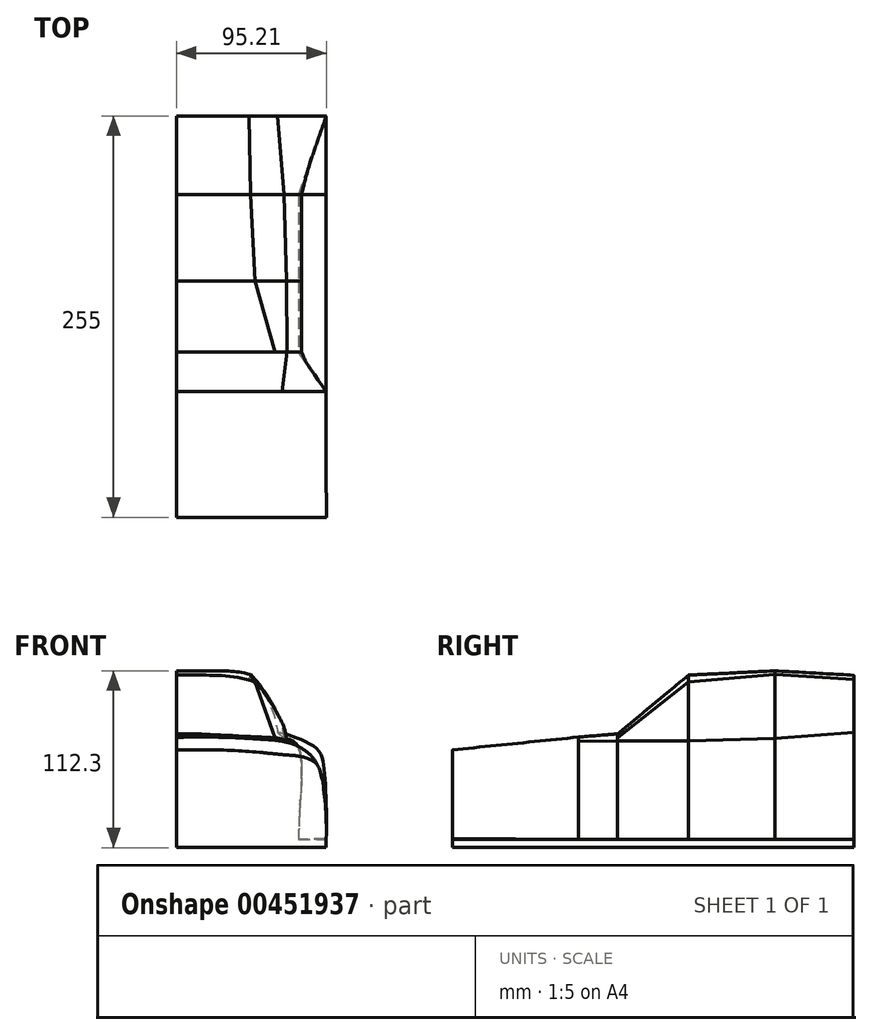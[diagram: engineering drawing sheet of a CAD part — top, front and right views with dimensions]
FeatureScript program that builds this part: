
annotation { "Feature Type Name" : "Feature", "Feature Type Description" : "" }
export const myFeature = defineFeature(function(context is Context, id is Id, definition is map)
    precondition{}
    {
        {
            var Q0;
            Q0=qCreatedBy(makeId("Front.planeOp"),FACE);
            cPlane(context, id + "F0", {"entities" : qUnion([Q0]), "cplaneType" : CPlaneType.OFFSET, "offset" : 25 * mm, "width" : 150 * mm, "height" : 150 * mm});
        }
        {
            var Q0;
            Q0=qCreatedBy(id+"F0.planeOp",FACE);
            cPlane(context, id + "F1", {"entities" : qUnion([Q0]), "cplaneType" : CPlaneType.OFFSET, "offset" : 55 * mm, "width" : 150 * mm, "height" : 150 * mm});
        }
        {
            var Q0;
            Q0=qCreatedBy(id+"F1.planeOp",FACE);
            var sketch = newSketch(context, id + "F2", { "sketchPlane" : qUnion([Q0])});
            skLineSegment(sketch, "E0", {"start": v(-56.2, -43.48) * mm, "end": v(38.8, -43.48) * mm});
            skLineSegment(sketch, "E1", {"start": v(-56.2, -43.48) * mm, "end": v(-56.2, 68.52) * mm});
            skFitSpline(sketch, "E2", {"points": [v(-56.2, 68.52) * mm, v(-28.09, 68.52) * mm, v(-9.15, 66.18) * mm], "startDerivative": vector(14.34, 0) * mm, "endDerivative": vector(49, -12.81) * mm});
            skFitSpline(sketch, "E3", {"points": [v(-9.15, 66.18) * mm, v(3.27, 49.99) * mm, v(10.5, 34.27) * mm, v(12.07, 25.62) * mm], "startDerivative": vector(39.03, -40.53) * mm, "endDerivative": vector(5.17, -25.63) * mm});
            skFitSpline(sketch, "E4", {"points": [v(12.07, 25.62) * mm, v(18.99, 23.1) * mm, v(23.1, 11.29) * mm, v(22.4, -13.75) * mm, v(21.25, -38.41) * mm], "startDerivative": vector(44.42, -4.76) * mm, "endDerivative": vector(-3.51, -107.92) * mm});
            skFitSpline(sketch, "E5", {"points": [v(21.25, -38.41) * mm, v(38.7, -38.41) * mm], "startDerivative": vector(17.45, 0) * mm, "endDerivative": vector(17.45, 0) * mm});
            skFitSpline(sketch, "E6", {"points": [v(38.7, -38.41) * mm, v(38.8, -43.48) * mm], "startDerivative": vector(0.15, -5.07) * mm, "endDerivative": vector(0.15, -5.07) * mm});
            skSolve(sketch);
        }
        {
            var Q0;
            Q0=qCreatedBy(id+"F1.planeOp",FACE);
            cPlane(context, id + "F3", {"entities" : qUnion([Q0]), "cplaneType" : CPlaneType.OFFSET, "offset" : 55 * mm, "width" : 150 * mm, "height" : 150 * mm});
        }
        {
            var Q0;
            Q0=qCreatedBy(id+"F3.planeOp",FACE);
            var sketch = newSketch(context, id + "F4", { "sketchPlane" : qUnion([Q0])});
            skLineSegment(sketch, "E7", {"start": v(-56.24, -43.48) * mm, "end": v(38.76, -43.48) * mm});
            skLineSegment(sketch, "E8", {"start": v(-56.24, -43.48) * mm, "end": v(-56.24, 65.86) * mm});
            skFitSpline(sketch, "E9", {"points": [v(-56.24, 65.86) * mm, v(-42, 65.86) * mm, v(-6.36, 61.62) * mm], "startDerivative": vector(26.6, 0) * mm, "endDerivative": vector(61.7, -20.82) * mm});
            skFitSpline(sketch, "E10", {"points": [v(-6.36, 61.62) * mm, v(2.01, 51.09) * mm, v(12.26, 32.17) * mm, v(13.8, 24.2) * mm], "startDerivative": vector(39.03, -40.53) * mm, "endDerivative": vector(5.17, -25.63) * mm});
            skFitSpline(sketch, "E11", {"points": [v(13.8, 24.2) * mm, v(20.09, 22) * mm, v(23.1, 11.29) * mm, v(22.4, -13.75) * mm, v(21.17, -38.41) * mm], "startDerivative": vector(44.42, -4.76) * mm, "endDerivative": vector(-3.51, -107.92) * mm});
            skFitSpline(sketch, "E12", {"points": [v(21.17, -38.41) * mm, v(38.7, -38.41) * mm], "startDerivative": vector(17.45, 0) * mm, "endDerivative": vector(17.45, 0) * mm});
            skFitSpline(sketch, "E13", {"points": [v(38.7, -38.41) * mm, v(38.76, -43.48) * mm], "startDerivative": vector(0.15, -5.07) * mm, "endDerivative": vector(0.15, -5.07) * mm});
            skSolve(sketch);
        }
        {
            var Q0;
            Q0=makeQuery(id+"F2.imprint","IMPRINT",FACE,{"disambiguationData":[TD([[makeQuery(id+"F2.imprint","IMPRINT",EDGE,{"derivedFrom":sQuery(id+"F2.wireOp",EDGE,"E0")}),1.0]])]});
            var Q1;
            Q1=makeQuery(id+"F4.imprint","IMPRINT",FACE,{"disambiguationData":[TD([[makeQuery(id+"F4.imprint","IMPRINT",EDGE,{"derivedFrom":sQuery(id+"F4.wireOp",EDGE,"E7")}),1.0]])]});
            loft(context, id + "F5", {"sheetProfilesArray" : [{ "sheetProfileEntities" : qUnion([Q0]) }, { "sheetProfileEntities" : qUnion([Q1]) }]});
        }
        {
            var Q0;
            Q0=qCreatedBy(id+"F3.planeOp",FACE);
            cPlane(context, id + "F6", {"entities" : qUnion([Q0]), "cplaneType" : CPlaneType.OFFSET, "offset" : 45 * mm, "width" : 150 * mm, "height" : 150 * mm});
        }
        {
            var Q0;
            Q0=qCreatedBy(id+"F6.planeOp",FACE);
            var sketch = newSketch(context, id + "F7", { "sketchPlane" : qUnion([Q0])});
            skLineSegment(sketch, "E14", {"start": v(-56.16, -43.48) * mm, "end": v(38.84, -43.48) * mm});
            skLineSegment(sketch, "E15", {"start": v(-56.16, -43.48) * mm, "end": v(-56.16, 28.45) * mm});
            skFitSpline(sketch, "E16", {"points": [v(-56.16, 28.45) * mm, v(-42.28, 28.45) * mm, v(6.24, 26.03) * mm], "startDerivative": vector(90.88, 0) * mm, "endDerivative": vector(48.69, -2.52) * mm});
            skFitSpline(sketch, "E17", {"points": [v(13.92, 24.12) * mm, v(19.67, 22.2) * mm, v(23.1, 11.29) * mm, v(22.4, -13.75) * mm, v(21.25, -38.41) * mm], "startDerivative": vector(53.36, -8.52) * mm, "endDerivative": vector(-3.51, -107.92) * mm});
            skFitSpline(sketch, "E18", {"points": [v(21.25, -38.41) * mm, v(38.7, -38.41) * mm], "startDerivative": vector(17.45, 0) * mm, "endDerivative": vector(17.45, 0) * mm});
            skFitSpline(sketch, "E19", {"points": [v(38.7, -38.41) * mm, v(38.84, -43.48) * mm], "startDerivative": vector(0.15, -5.07) * mm, "endDerivative": vector(0.15, -5.07) * mm});
            skFitSpline(sketch, "E20", {"points": [v(6.24, 26.03) * mm, v(13.92, 24.12) * mm], "startDerivative": vector(7.78, -0.7) * mm, "endDerivative": vector(7.95, -3.49) * mm});
            skSolve(sketch);
        }
        {
            var Q1;
            Q1=makeQuery(id+"F5.opLoft","CAP_FACE",FACE,{"disambiguationData":[OSD([makeQuery(id+"F4.imprint","IMPRINT",FACE,{"disambiguationData":[TD([[makeQuery(id+"F4.imprint","IMPRINT",EDGE,{"derivedFrom":sQuery(id+"F4.wireOp",EDGE,"E7")}),1.0]])]})])],"isStart":true});
            var Q2;
            Q2=makeQuery(id+"F7.imprint","IMPRINT",FACE,{"disambiguationData":[TD([[makeQuery(id+"F7.imprint","IMPRINT",EDGE,{"derivedFrom":sQuery(id+"F7.wireOp",EDGE,"E14")}),1.0]])]});
            loft(context, id + "F8", {"operationType" : NewBodyOperationType.ADD, "sheetProfilesArray" : [{ "sheetProfileEntities" : qUnion([Q1]) }, { "sheetProfileEntities" : qUnion([Q2]) }]});
        }
        {
            var Q0;
            Q0=qCreatedBy(id+"F6.planeOp",FACE);
            cPlane(context, id + "F9", {"entities" : qUnion([Q0]), "cplaneType" : CPlaneType.OFFSET, "offset" : 25 * mm, "width" : 150 * mm, "height" : 150 * mm});
        }
        {
            var Q0;
            Q0=qCreatedBy(id+"F9.planeOp",FACE);
            var sketch = newSketch(context, id + "F10", { "sketchPlane" : qUnion([Q0])});
            skLineSegment(sketch, "E21", {"start": v(-56.14, -43.49) * mm, "end": v(38.86, -43.49) * mm});
            skLineSegment(sketch, "E22", {"start": v(-56.14, -43.49) * mm, "end": v(-56.14, 26.42) * mm});
            skFitSpline(sketch, "E23", {"points": [v(-56.14, 26.42) * mm, v(-29.47, 26.42) * mm, v(1.75, 24.92) * mm], "startDerivative": vector(49.24, 0) * mm, "endDerivative": vector(48.69, -2.52) * mm});
            skFitSpline(sketch, "E24", {"points": [v(10.97, 23.8) * mm, v(19.2, 21.48) * mm, v(28.71, 15.27) * mm, v(35.59, 1.92) * mm, v(38.67, -38.4) * mm], "startDerivative": vector(52.32, -10.37) * mm, "endDerivative": vector(-3.51, -107.92) * mm});
            skFitSpline(sketch, "E25", {"points": [v(38.7, -38.4) * mm, v(38.86, -43.49) * mm], "startDerivative": vector(0.15, -5.07) * mm, "endDerivative": vector(0.15, -5.07) * mm});
            skFitSpline(sketch, "E26", {"points": [v(1.75, 24.92) * mm, v(10.97, 23.8) * mm], "startDerivative": vector(7.78, -0.7) * mm, "endDerivative": vector(14.17, -2.75) * mm});
            skLineSegment(sketch, "E27", {"start": v(38.67, -38.4) * mm, "end": v(38.7, -38.4) * mm});
            skSolve(sketch);
        }
        {
            var Q1;
            Q1=makeQuery(id+"F10.imprint","IMPRINT",FACE,{"disambiguationData":[TD([[makeQuery(id+"F10.imprint","IMPRINT",EDGE,{"derivedFrom":sQuery(id+"F10.wireOp",EDGE,"E21")}),1.0]])]});
            var Q2;
            Q2=makeQuery(id+"F7.imprint","IMPRINT",FACE,{"disambiguationData":[TD([[makeQuery(id+"F7.imprint","IMPRINT",EDGE,{"derivedFrom":sQuery(id+"F7.wireOp",EDGE,"E14")}),1.0]])]});
            loft(context, id + "F11", {"operationType" : NewBodyOperationType.ADD, "sheetProfilesArray" : [{ "sheetProfileEntities" : qUnion([Q1]) }, { "sheetProfileEntities" : qUnion([Q2]) }]});
        }
        {
            var Q0;
            Q0=qCreatedBy(id+"F9.planeOp",FACE);
            cPlane(context, id + "F12", {"entities" : qUnion([Q0]), "cplaneType" : CPlaneType.OFFSET, "offset" : 80 * mm, "width" : 150 * mm, "height" : 150 * mm});
        }
        {
            var Q0;
            Q0=qCreatedBy(id+"F12.planeOp",FACE);
            var sketch = newSketch(context, id + "F13", { "sketchPlane" : qUnion([Q0])});
            skLineSegment(sketch, "E28", {"start": v(-56.16, -43.52) * mm, "end": v(38.84, -43.52) * mm});
            skLineSegment(sketch, "E29", {"start": v(-56.16, -43.52) * mm, "end": v(-56.16, 18.26) * mm});
            skFitSpline(sketch, "E30", {"points": [v(-56.16, 18.26) * mm, v(-26.52, 18.26) * mm, v(-1.45, 16.61) * mm], "startDerivative": vector(49.26, -1.16) * mm, "endDerivative": vector(48.66, -3.24) * mm});
            skFitSpline(sketch, "E31", {"points": [v(17.41, 14.88) * mm, v(27.24, 12.92) * mm, v(32.34, 9.77) * mm, v(35.33, 4.04) * mm, v(38.88, -37.9) * mm], "startDerivative": vector(38.35, -2.8) * mm, "endDerivative": vector(-3.51, -107.92) * mm});
            skFitSpline(sketch, "E32", {"points": [v(38.88, -38.45) * mm, v(38.84, -43.52) * mm], "startDerivative": vector(0.15, -5.07) * mm, "endDerivative": vector(0.15, -5.07) * mm});
            skFitSpline(sketch, "E33", {"points": [v(-1.45, 16.61) * mm, v(17.41, 14.88) * mm], "startDerivative": vector(20.28, -2.36) * mm, "endDerivative": vector(19.1, -1.41) * mm});
            skLineSegment(sketch, "E34", {"start": v(38.88, -37.9) * mm, "end": v(38.88, -38.45) * mm});
            skSolve(sketch);
        }
        {
            var Q1;
            Q1 = qSketchRegion(id + "F13", true);
            var Q2;
            Q2 = qSketchRegion(id + "F10", true);
            loft(context, id + "F14", {"operationType" : NewBodyOperationType.ADD, "sheetProfilesArray" : [{ "sheetProfileEntities" : qUnion([Q1]) }, { "sheetProfileEntities" : qUnion([Q2]) }]});
        }
        {
            var Q0;
            Q0=qCreatedBy(id+"F1.planeOp",FACE);
            cPlane(context, id + "F15", {"entities" : qUnion([Q0]), "cplaneType" : CPlaneType.OFFSET, "offset" : 50 * mm, "oppositeDirection" : true, "width" : 150 * mm, "height" : 150 * mm});
        }
        {
            var Q0;
            Q0=qCreatedBy(id+"F15.planeOp",FACE);
            var sketch = newSketch(context, id + "F16", { "sketchPlane" : qUnion([Q0])});
            skLineSegment(sketch, "E35", {"start": v(-56.13, -43.72) * mm, "end": v(38.87, -43.72) * mm});
            skLineSegment(sketch, "E36", {"start": v(-56.13, -43.72) * mm, "end": v(-56.13, 65.71) * mm});
            skFitSpline(sketch, "E37", {"points": [v(-56.13, 65.71) * mm, v(-31.5, 65.71) * mm, v(-10.12, 63.16) * mm], "startDerivative": vector(14.35, 0) * mm, "endDerivative": vector(49, -12.81) * mm});
            skFitSpline(sketch, "E38", {"points": [v(-10.12, 63.16) * mm, v(1.47, 50.38) * mm, v(6.33, 37.93) * mm, v(8.07, 29.6) * mm], "startDerivative": vector(36.79, -22.63) * mm, "endDerivative": vector(5.17, -25.63) * mm});
            skFitSpline(sketch, "E39", {"points": [v(8.07, 29.6) * mm, v(15.02, 27.83) * mm, v(32.97, 19.05) * mm, v(37.58, 6.35) * mm, v(38.78, -38.25) * mm], "startDerivative": vector(44.42, -4.76) * mm, "endDerivative": vector(-4.6, -144.45) * mm});
            skFitSpline(sketch, "E40", {"points": [v(38.77, -38.42) * mm, v(38.87, -43.72) * mm], "startDerivative": vector(0.15, -5.07) * mm, "endDerivative": vector(0.15, -5.07) * mm});
            skLineSegment(sketch, "E41", {"start": v(38.78, -38.25) * mm, "end": v(38.77, -38.42) * mm});
            skSolve(sketch);
        }
        {
            var Q1;
            Q1 = qSketchRegion(id + "F16", true);
            var Q2;
            Q2=makeQuery(id+"F5.opLoft","CAP_FACE",FACE,{"disambiguationData":[OSD([makeQuery(id+"F2.imprint","IMPRINT",FACE,{"disambiguationData":[TD([[makeQuery(id+"F2.imprint","IMPRINT",EDGE,{"derivedFrom":sQuery(id+"F2.wireOp",EDGE,"E0")}),1.0]])]})])],"isStart":true});
            loft(context, id + "F17", {"operationType" : NewBodyOperationType.ADD, "sheetProfilesArray" : [{ "sheetProfileEntities" : qUnion([Q1]) }, { "sheetProfileEntities" : qUnion([Q2]) }]});
        }
    });
